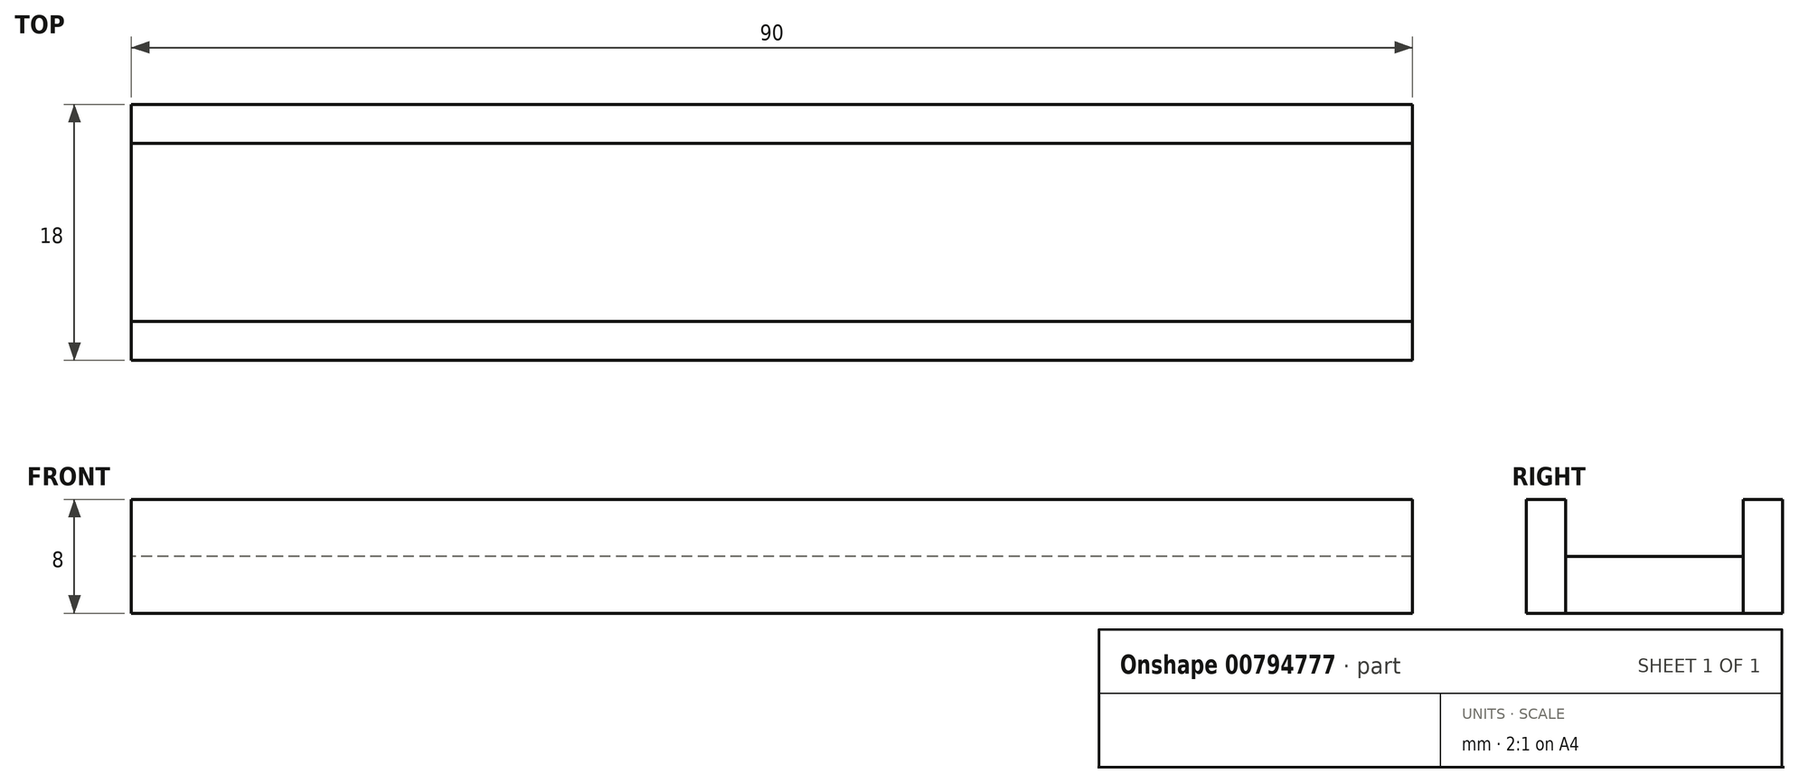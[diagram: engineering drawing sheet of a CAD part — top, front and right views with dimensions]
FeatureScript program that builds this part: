
annotation { "Feature Type Name" : "Feature", "Feature Type Description" : "" }
export const myFeature = defineFeature(function(context is Context, id is Id, definition is map)
    precondition{}
    {
        {
            var Q0;
            Q0=qCreatedBy(makeId("Top.planeOp"),FACE);
            var sketch = newSketch(context, id + "F0", { "sketchPlane" : qUnion([Q0])});
            skLineSegment(sketch, "E0.bottom", {"start": v(45, -6.25) * mm, "end": v(-45, -6.25) * mm});
            skLineSegment(sketch, "E0.top", {"start": v(45, 6.25) * mm, "end": v(-45, 6.25) * mm});
            skLineSegment(sketch, "E0.left", {"start": v(45, -6.25) * mm, "end": v(45, 6.25) * mm});
            skLineSegment(sketch, "E0.right", {"start": v(-45, -6.25) * mm, "end": v(-45, 6.25) * mm});
            skPoint(sketch, "E0.middle", {"position": v(0, 0) * mm});
            skLineSegment(sketch, "E1.bottom", {"start": v(-45, -9) * mm, "end": v(45, -9) * mm});
            skLineSegment(sketch, "E1.top", {"start": v(-45, 9) * mm, "end": v(45, 9) * mm});
            skLineSegment(sketch, "E1.left", {"start": v(-45, -9) * mm, "end": v(-45, 9) * mm});
            skLineSegment(sketch, "E1.right", {"start": v(45, -9) * mm, "end": v(45, 9) * mm});
            skSolve(sketch);
        }
        {
            var Q0;
            {var subQ0=sQuery(id+"F0.wireOp",EDGE,"E0.top");Q0=makeQuery(id+"F0.imprint","IMPRINT",FACE,{"disambiguationData":[TD([[makeQuery(id+"F0.imprint","IMPRINT",EDGE,{"derivedFrom":subQ0}),-1.0]])]});}
            var Q1;
            {var subQ0=sQuery(id+"F0.wireOp",EDGE,"E0.bottom");Q1=makeQuery(id+"F0.imprint","IMPRINT",FACE,{"disambiguationData":[TD([[makeQuery(id+"F0.imprint","IMPRINT",EDGE,{"derivedFrom":subQ0}),1.0]])]});}
            extrude(context, id + "F1", {"entities" : qUnion([Q0, Q1]), "depth" : 8 * mm, "offsetDistance" : 25 * mm});
        }
        {
            var Q0;
            {var subQ0=sQuery(id+"F0.wireOp",EDGE,"E0.bottom");Q0=makeQuery(id+"F0.imprint","IMPRINT",FACE,{"disambiguationData":[TD([[makeQuery(id+"F0.imprint","IMPRINT",EDGE,{"derivedFrom":subQ0}),-1.0]])]});}
            extrude(context, id + "F2", {"entities" : qUnion([Q0]), "depth" : 4 * mm, "offsetDistance" : 25 * mm});
        }
    });
